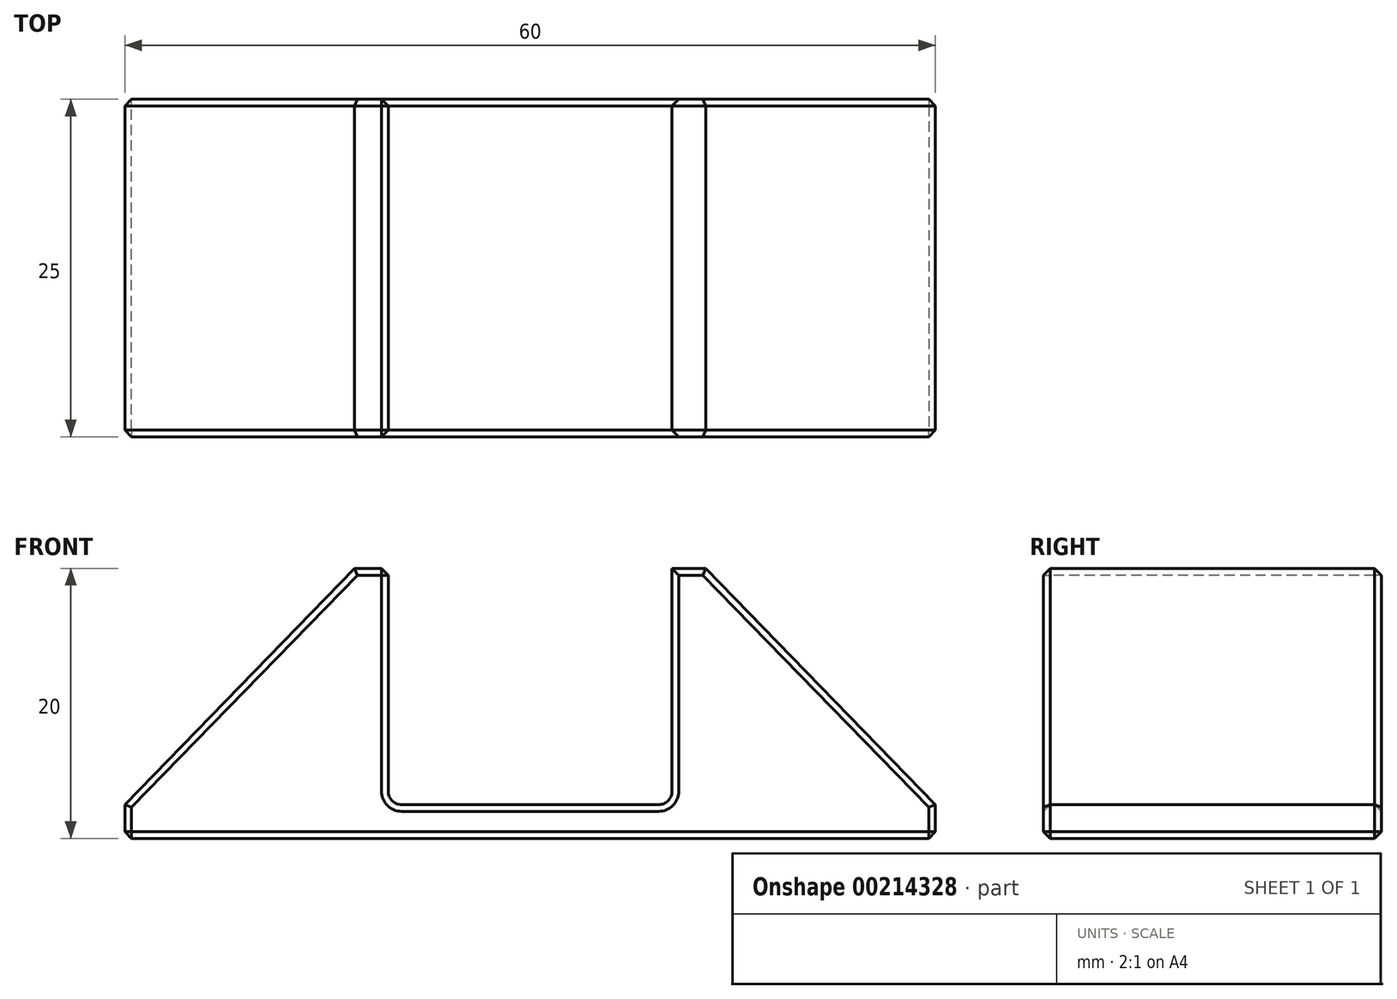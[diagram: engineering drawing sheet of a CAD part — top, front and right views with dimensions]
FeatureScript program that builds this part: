
annotation { "Feature Type Name" : "Feature", "Feature Type Description" : "" }
export const myFeature = defineFeature(function(context is Context, id is Id, definition is map)
    precondition{}
    {
        {
            var Q0;
            Q0=qCreatedBy(makeId("Top.planeOp"),FACE);
            var sketch = newSketch(context, id + "F0", { "sketchPlane" : qUnion([Q0])});
            skLineSegment(sketch, "E0.bottom", {"start": v(30, 12.5) * mm, "end": v(-30, 12.5) * mm});
            skLineSegment(sketch, "E0.top", {"start": v(30, -12.5) * mm, "end": v(-30, -12.5) * mm});
            skLineSegment(sketch, "E0.left", {"start": v(30, 12.5) * mm, "end": v(30, -12.5) * mm});
            skLineSegment(sketch, "E0.right", {"start": v(-30, 12.5) * mm, "end": v(-30, -12.5) * mm});
            skPoint(sketch, "E0.middle", {"position": v(0, 0) * mm});
            skSolve(sketch);
        }
        {
            var Q0;
            Q0 = qSketchRegion(id + "F0", true);
            extrude(context, id + "F1", {"entities" : qUnion([Q0]), "depth" : 20 * mm, "offsetDistance" : 25 * mm});
        }
        {
            var Q0;
            Q0=makeQuery(id+"F1.opExtrude","SWEPT_FACE",FACE,{"disambiguationData":[OSD([sQuery(id+"F0.wireOp",EDGE,"E0.top")])]});
            var sketch = newSketch(context, id + "F2", { "sketchPlane" : qUnion([Q0])});
            skLineSegment(sketch, "E1.bottom", {"start": v(10.5, 20) * mm, "end": v(-10.5, 20) * mm});
            skLineSegment(sketch, "E1.top", {"start": v(10.5, 2.5) * mm, "end": v(-10.5, 2.5) * mm});
            skLineSegment(sketch, "E1.left", {"start": v(10.5, 20) * mm, "end": v(10.5, 2.5) * mm});
            skLineSegment(sketch, "E1.right", {"start": v(-10.5, 20) * mm, "end": v(-10.5, 2.5) * mm});
            skPoint(sketch, "E1.middle", {"position": v(0, 11.25) * mm});
            skLineSegment(sketch, "E2", {"start": v(-13, 20) * mm, "end": v(-30, 2.5) * mm});
            skLineSegment(sketch, "E3", {"start": v(-13, 20) * mm, "end": v(-30, 20) * mm});
            skLineSegment(sketch, "E4", {"start": v(-30, 20) * mm, "end": v(-30, 2.5) * mm});
            skLineSegment(sketch, "E5.MirrorCS", {"start": v(30, 20) * mm, "end": v(30, 2.5) * mm});
            skLineSegment(sketch, "E6.MirrorCS", {"start": v(13, 20) * mm, "end": v(30, 2.5) * mm});
            skLineSegment(sketch, "E7.MirrorCS", {"start": v(13, 20) * mm, "end": v(30, 20) * mm});
            skSolve(sketch);
        }
        {
            var Q0;
            Q0 = qSketchRegion(id + "F2", true);
            extrude(context, id + "F3", {"entities" : qUnion([Q0]), "operationType" : NewBodyOperationType.REMOVE, "endBound" : BoundingType.THROUGH_ALL, "oppositeDirection" : true, "depth" : 25 * mm, "offsetDistance" : 25 * mm});
        }
        {
            var Q0;
            Q0=makeQuery(id+"F3.boolean.opBoolean","COPY",EDGE,{"derivedFrom":makeQuery(id+"F3.opExtrude","SWEPT_EDGE",EDGE,{"disambiguationData":[OSD([sQuery(id+"F2.wireOp",EDGE,"E1.top"),sQuery(id+"F2.wireOp",EDGE,"E1.right")])]})});
            var Q1;
            Q1=makeQuery(id+"F3.boolean.opBoolean","COPY",EDGE,{"derivedFrom":makeQuery(id+"F3.opExtrude","SWEPT_EDGE",EDGE,{"disambiguationData":[OSD([sQuery(id+"F2.wireOp",EDGE,"E1.top"),sQuery(id+"F2.wireOp",EDGE,"E1.left")])]})});
            var Q2;
            Q2=makeQuery(id+"F3.boolean.opBoolean","COPY",EDGE,{"derivedFrom":makeQuery(id+"F3.opExtrude","SWEPT_EDGE",EDGE,{"disambiguationData":[OSD([sQuery(id+"F0.wireOp",EDGE,"E0.top"),sQuery(id+"F0.wireOp",EDGE,"E0.right"),sQuery(id+"F2.wireOp",EDGE,"E2"),sQuery(id+"F2.wireOp",EDGE,"E4")])]})});
            var Q3;
            Q3=makeQuery(id+"F3.boolean.opBoolean","COPY",EDGE,{"derivedFrom":makeQuery(id+"F3.opExtrude","SWEPT_EDGE",EDGE,{"disambiguationData":[OSD([sQuery(id+"F0.wireOp",EDGE,"E0.top"),sQuery(id+"F0.wireOp",EDGE,"E0.left"),sQuery(id+"F2.wireOp",EDGE,"E5.MirrorCS"),sQuery(id+"F2.wireOp",EDGE,"E6.MirrorCS")])]})});
            fillet(context, id + "F4", {"entities" : qUnion([Q0, Q1, Q2, Q3]), "radius" : 1 * mm, "tangentPropagation" : true, "allowEdgeOverflow" : false});
        }
        {
            var Q0;
            Q0=makeQuery(id+"F1.opExtrude","CAP_EDGE",EDGE,{"disambiguationData":[OSD([sQuery(id+"F0.wireOp",EDGE,"E0.top")])],"isStart":true});
            var Q1;
            Q1=makeQuery(id+"F1.opExtrude","CAP_EDGE",EDGE,{"disambiguationData":[OSD([sQuery(id+"F0.wireOp",EDGE,"E0.left")])],"isStart":true});
            var Q2;
            Q2=makeQuery(id+"F1.opExtrude","CAP_EDGE",EDGE,{"disambiguationData":[OSD([sQuery(id+"F0.wireOp",EDGE,"E0.bottom")])],"isStart":true});
            var Q3;
            Q3=makeQuery(id+"F1.opExtrude","CAP_EDGE",EDGE,{"disambiguationData":[OSD([sQuery(id+"F0.wireOp",EDGE,"E0.right")])],"isStart":true});
            var Q4;
            Q4=makeQuery(id+"F3.boolean.opBoolean","COPY",EDGE,{"derivedFrom":makeQuery(id+"F3.opExtrude","SWEPT_EDGE",EDGE,{"disambiguationData":[OSD([sQuery(id+"F0.wireOp",EDGE,"E0.top"),sQuery(id+"F2.wireOp",EDGE,"E1.bottom"),sQuery(id+"F2.wireOp",EDGE,"E1.right")])]})});
            var Q5;
            Q5=makeQuery(id+"F3.boolean.opBoolean","COPY",EDGE,{"derivedFrom":makeQuery(id+"F3.opExtrude","SWEPT_EDGE",EDGE,{"disambiguationData":[OSD([sQuery(id+"F0.wireOp",EDGE,"E0.top"),sQuery(id+"F2.wireOp",EDGE,"E1.bottom"),sQuery(id+"F2.wireOp",EDGE,"E1.left")])]})});
            var Q6;
            Q6=makeQuery(id+"F1.opExtrude","SWEPT_FACE",FACE,{"disambiguationData":[OSD([sQuery(id+"F0.wireOp",EDGE,"E0.top")])]});
            var Q7;
            Q7=makeQuery(id+"F1.opExtrude","SWEPT_FACE",FACE,{"disambiguationData":[OSD([sQuery(id+"F0.wireOp",EDGE,"E0.bottom")])]});
            chamfer(context, id + "F5", {"entities" : qUnion([Q0, Q1, Q2, Q3, Q4, Q5, Q6, Q7]), "width" : 0.5 * mm, "tangentPropagation" : true});
        }
    });
